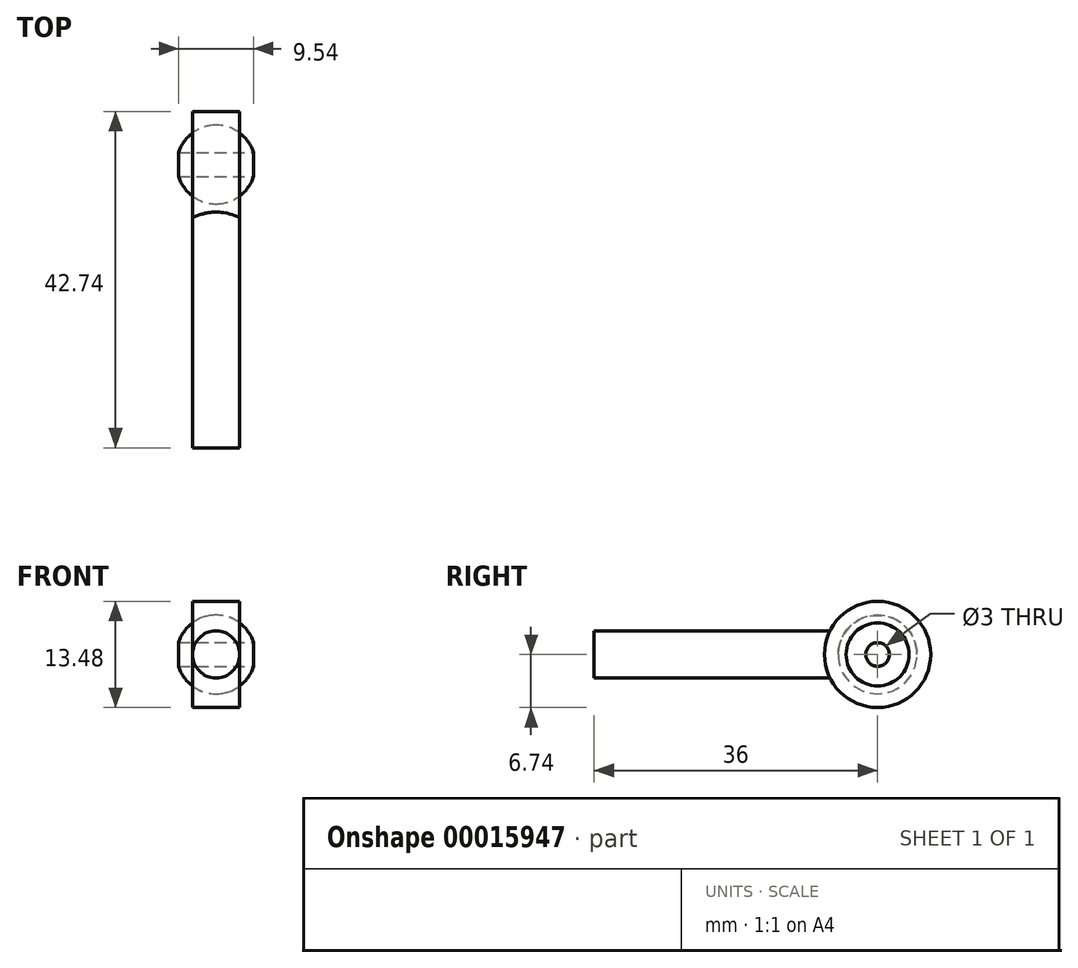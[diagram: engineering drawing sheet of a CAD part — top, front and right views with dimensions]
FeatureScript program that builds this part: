
annotation { "Feature Type Name" : "Feature", "Feature Type Description" : "" }
export const myFeature = defineFeature(function(context is Context, id is Id, definition is map)
    precondition{}
    {
        {
            var Q0;
            Q0=qCreatedBy(makeId("Top.planeOp"),FACE);
            var sketch = newSketch(context, id + "F0", { "sketchPlane" : qUnion([Q0])});
            skCircle(sketch, "E0", {"center": v(0, 0) * mm, "radius": 5 * mm});
            skLineSegment(sketch, "E1", {"start": v(0, 5) * mm, "end": v(0, -5) * mm});
            skLineSegment(sketch, "E2", {"start": v(-5, 0) * mm, "end": v(5, 0) * mm});
            skSolve(sketch);
        }
        {
            var Q0;
            {var subQ0=sQuery(id+"F0.wireOp",EDGE,"E1");Q0=makeQuery(id+"F0.imprint","IMPRINT",FACE,{"disambiguationData":[TD([[makeQuery(id+"F0.imprint","IMPRINT",EDGE,{"derivedFrom":subQ0}),1.0]])]});}
            var Q1;
            Q1=sQuery(id+"F0.wireOp",EDGE,"E1");
            revolve(context, id + "F1", {"entities" : qUnion([Q0]), "axis" : qUnion([Q1]), "revolveType" : RevolveType.FULL});
        }
        {
            var Q0;
            Q0=qCreatedBy(makeId("Right.planeOp"),FACE);
            var sketch = newSketch(context, id + "F2", { "sketchPlane" : qUnion([Q0])});
            skCircle(sketch, "E3", {"center": v(0, 0) * mm, "radius": 6.74 * mm});
            skSolve(sketch);
        }
        {
            var Q0;
            Q0=makeQuery(id+"F2.imprint","IMPRINT",FACE,{"disambiguationData":[TD([[makeQuery(id+"F2.imprint","IMPRINT",EDGE,{"derivedFrom":sQuery(id+"F2.wireOp",EDGE,"E3")}),1.0]])]});
            extrude(context, id + "F3", {"entities" : qUnion([Q0]), "depth" : 6 * mm, "symmetric" : true});
        }
        {
            var Q0;
            Q0=makeQuery(id+"F1.opRevolve","SWEPT_BODY",BODY,{"disambiguationData":[OSD([sQuery(id+"F0.wireOp",EDGE,"E0"),sQuery(id+"F0.wireOp",EDGE,"E1")])]});
            var Q1;
            Q1=makeQuery(id+"F3.opExtrude","SWEPT_BODY",BODY,{"disambiguationData":[OSD([sQuery(id+"F2.wireOp",EDGE,"E3")])]});
            booleanBodies(context, id + "F4", {"operationType" : BooleanOperationType.SUBTRACTION, "tools" : qUnion([Q0]), "targets" : qUnion([Q1]), "keepTools" : true});
        }
        {
            var Q0;
            Q0=qCreatedBy(makeId("Right.planeOp"),FACE);
            var sketch = newSketch(context, id + "F5", { "sketchPlane" : qUnion([Q0])});
            skCircle(sketch, "E4", {"center": v(0, 0) * mm, "radius": 1.5 * mm});
            skSolve(sketch);
        }
        {
            var Q0;
            Q0 = qSketchRegion(id + "F5", true);
            extrude(context, id + "F6", {"entities" : qUnion([Q0]), "operationType" : NewBodyOperationType.REMOVE, "oppositeDirection" : true, "depth" : 25 * mm, "symmetric" : true});
        }
        {
            var Q0;
            Q0=qCreatedBy(makeId("Front.planeOp"),FACE);
            cPlane(context, id + "F7", {"entities" : qUnion([Q0]), "cplaneType" : CPlaneType.OFFSET, "offset" : 6 * mm, "width" : 150 * mm, "height" : 150 * mm});
        }
        {
            var Q0;
            Q0=qCreatedBy(id+"F7.planeOp",FACE);
            var sketch = newSketch(context, id + "F8", { "sketchPlane" : qUnion([Q0])});
            skCircle(sketch, "E5", {"center": v(0, 0) * mm, "radius": 3 * mm});
            skSolve(sketch);
        }
        {
            var Q0;
            Q0 = qSketchRegion(id + "F8", true);
            extrude(context, id + "F9", {"entities" : qUnion([Q0]), "operationType" : NewBodyOperationType.ADD, "depth" : 30 * mm});
        }
    });
